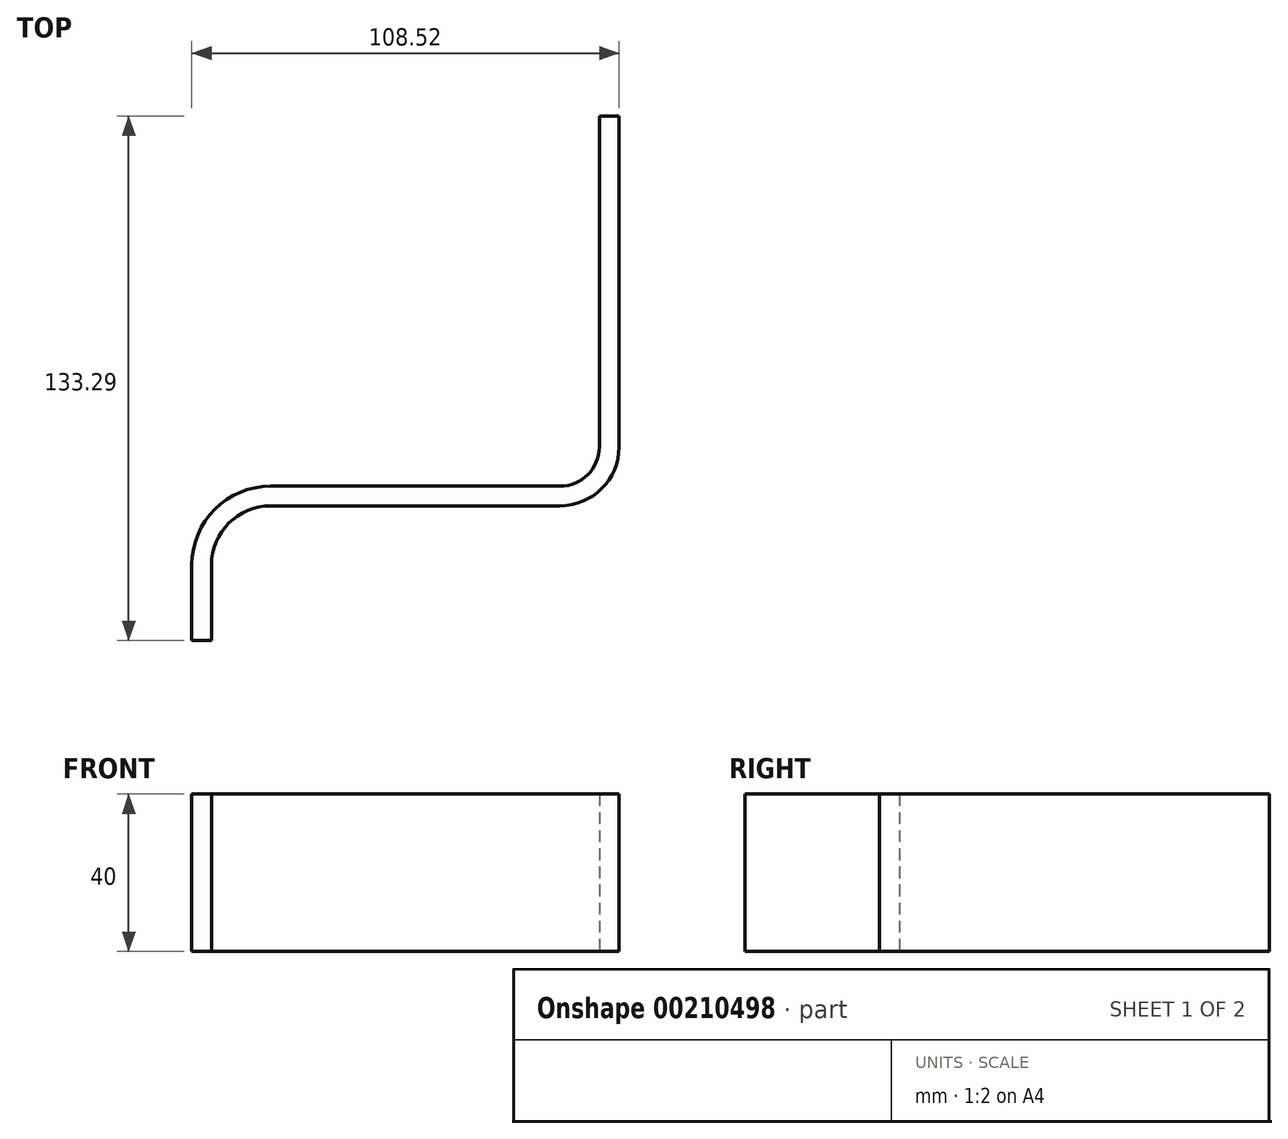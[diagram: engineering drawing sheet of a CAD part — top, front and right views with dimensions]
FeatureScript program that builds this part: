
annotation { "Feature Type Name" : "Feature", "Feature Type Description" : "" }
export const myFeature = defineFeature(function(context is Context, id is Id, definition is map)
    precondition{}
    {
        {
            var Q0;
            Q0=qCreatedBy(makeId("Top.planeOp"),FACE);
            var sketch = newSketch(context, id + "F0", { "sketchPlane" : qUnion([Q0])});
            skLineSegment(sketch, "E0", {"start": v(0, 0) * mm, "end": v(0, 19.23) * mm});
            skArc(sketch, "E1", {"start": v(0, 19.23) * mm, "mid": v(5.86, 33.37) * mm, "end": v(20, 39.23) * mm});
            skLineSegment(sketch, "E2", {"start": v(20, 39.23) * mm, "end": v(93.52, 39.23) * mm});
            skArc(sketch, "E3", {"start": v(93.52, 39.23) * mm, "mid": v(100.6, 42.16) * mm, "end": v(103.52, 49.23) * mm});
            skLineSegment(sketch, "E4", {"start": v(103.52, 49.23) * mm, "end": v(103.52, 133.29) * mm});
            skLineSegment(sketch, "E5.0", {"start": v(108.52, 49.23) * mm, "end": v(108.52, 133.29) * mm});
            skLineSegment(sketch, "E5.1", {"start": v(5, 0) * mm, "end": v(5, 19.23) * mm});
            skArc(sketch, "E5.2", {"start": v(5, 19.23) * mm, "mid": v(9.4, 29.84) * mm, "end": v(20, 34.23) * mm});
            skLineSegment(sketch, "E5.3", {"start": v(20, 34.23) * mm, "end": v(93.52, 34.23) * mm});
            skArc(sketch, "E5.4", {"start": v(93.52, 34.23) * mm, "mid": v(104.13, 38.62) * mm, "end": v(108.52, 49.23) * mm});
            skLineSegment(sketch, "E6", {"start": v(103.52, 133.29) * mm, "end": v(108.52, 133.29) * mm});
            skLineSegment(sketch, "E7", {"start": v(0, 0) * mm, "end": v(5, 0) * mm});
            skSolve(sketch);
        }
        {
            var Q0;
            Q0 = qSketchRegion(id + "F0", true);
            var Q1;
            Q1=makeQuery(id+"F0.imprint","IMPRINT",FACE,{"disambiguationData":[TD([[makeQuery(id+"F0.imprint","IMPRINT",EDGE,{"derivedFrom":sQuery(id+"F0.wireOp",EDGE,"E0")}),-1.0]])]});
            extrude(context, id + "F1", {"entities" : qUnion([Q0, Q1]), "depth" : 40 * mm});
        }
    });
